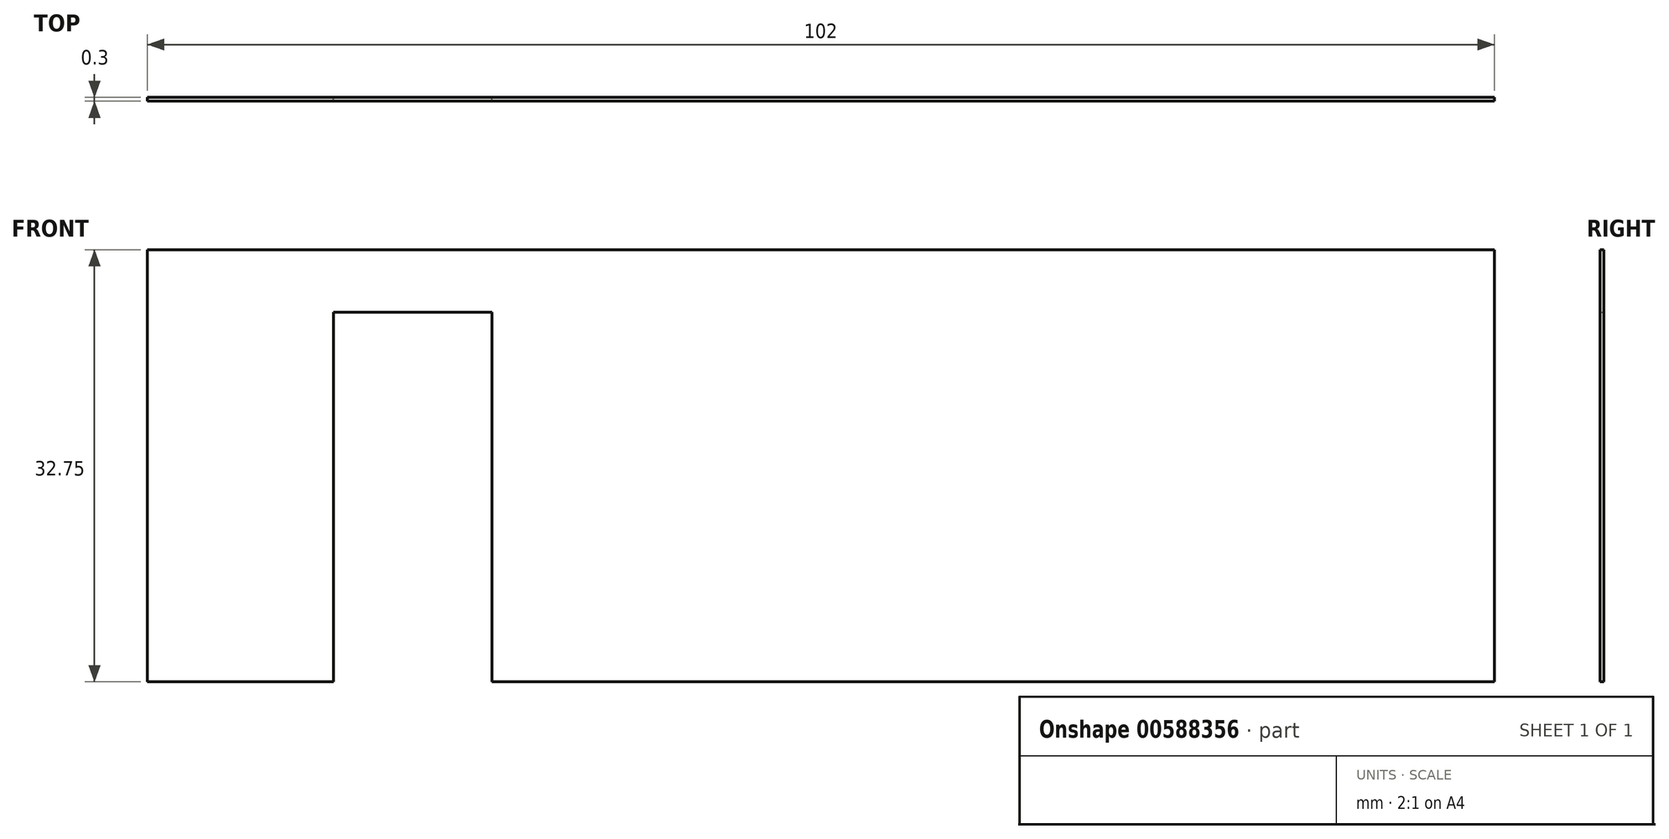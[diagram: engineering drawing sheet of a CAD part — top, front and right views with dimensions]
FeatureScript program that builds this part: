
annotation { "Feature Type Name" : "Feature", "Feature Type Description" : "" }
export const myFeature = defineFeature(function(context is Context, id is Id, definition is map)
    precondition{}
    {
        {
            var Q0;
            Q0=qCreatedBy(makeId("Front.planeOp"),FACE);
            var sketch = newSketch(context, id + "F0", { "sketchPlane" : qUnion([Q0])});
            skLineSegment(sketch, "E0", {"start": v(174.23, 57.64) * mm, "end": v(72.23, 57.64) * mm});
            skLineSegment(sketch, "E1", {"start": v(72.23, 57.64) * mm, "end": v(72.23, 90.4) * mm});
            skLineSegment(sketch, "E2", {"start": v(72.23, 90.4) * mm, "end": v(174.23, 90.4) * mm});
            skLineSegment(sketch, "E3", {"start": v(72.23, 57.64) * mm, "end": v(72.23, 34.9) * mm});
            skLineSegment(sketch, "E4", {"start": v(72.23, 34.9) * mm, "end": v(174.23, 34.9) * mm});
            skLineSegment(sketch, "E5", {"start": v(174.23, 34.9) * mm, "end": v(174.23, 57.64) * mm});
            skLineSegment(sketch, "E6", {"start": v(72.23, 34.9) * mm, "end": v(103.23, 34.9) * mm});
            skLineSegment(sketch, "E7", {"start": v(174.23, 57.64) * mm, "end": v(174.23, 90.4) * mm});
            skLineSegment(sketch, "E8", {"start": v(174.23, 34.9) * mm, "end": v(170.23, 34.9) * mm});
            skLineSegment(sketch, "E9", {"start": v(170.23, 34.9) * mm, "end": v(170.23, 90.4) * mm});
            skLineSegment(sketch, "E10", {"start": v(72.23, 34.9) * mm, "end": v(77.23, 34.9) * mm});
            skLineSegment(sketch, "E11", {"start": v(77.23, 34.9) * mm, "end": v(77.23, 90.4) * mm});
            skLineSegment(sketch, "E12", {"start": v(174.23, 57.64) * mm, "end": v(170.23, 57.64) * mm});
            skLineSegment(sketch, "E13", {"start": v(170.23, 57.64) * mm, "end": v(123.23, 57.64) * mm});
            skLineSegment(sketch, "E14", {"start": v(123.23, 57.64) * mm, "end": v(123.23, 34.9) * mm});
            skLineSegment(sketch, "E15", {"start": v(72.23, 57.64) * mm, "end": v(77.23, 57.64) * mm});
            skLineSegment(sketch, "E16", {"start": v(77.23, 57.64) * mm, "end": v(86.33, 57.64) * mm});
            skLineSegment(sketch, "E17", {"start": v(86.33, 57.64) * mm, "end": v(86.33, 85.64) * mm});
            skLineSegment(sketch, "E18", {"start": v(86.33, 85.64) * mm, "end": v(98.33, 85.64) * mm});
            skLineSegment(sketch, "E19", {"start": v(98.33, 85.64) * mm, "end": v(98.33, 57.64) * mm});
            skLineSegment(sketch, "E20", {"start": v(98.33, 57.64) * mm, "end": v(86.33, 57.64) * mm});
            skSolve(sketch);
        }
        {
            var Q0;
            {var subQ0=sQuery(id+"F0.wireOp",EDGE,"E1");Q0=makeQuery(id+"F0.imprint","IMPRINT",FACE,{"disambiguationData":[TD([[makeQuery(id+"F0.imprint","IMPRINT",EDGE,{"derivedFrom":subQ0}),-1.0]])]});}
            var Q1;
            Q1=makeQuery(id+"F0.imprint","IMPRINT",FACE,{"disambiguationData":[TD([[makeQuery(id+"F0.imprint","IMPRINT",EDGE,{"derivedFrom":sQuery(id+"F0.wireOp",EDGE,"E0")}),-1.0]])]});
            var Q2;
            {var subQ0=sQuery(id+"F0.wireOp",EDGE,"E7");Q2=makeQuery(id+"F0.imprint","IMPRINT",FACE,{"disambiguationData":[TD([[makeQuery(id+"F0.imprint","IMPRINT",EDGE,{"derivedFrom":subQ0}),1.0]])]});}
            extrude(context, id + "F1", {"entities" : qUnion([Q0, Q1, Q2]), "depth" : .3 * mm, "offsetDistance" : 25 * mm});
        }
    });
